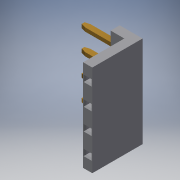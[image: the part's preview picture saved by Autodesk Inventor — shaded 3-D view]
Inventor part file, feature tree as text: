
AUTODESK INVENTOR PART (.ipt)
format: ipt  version: 2018.3 (Build 223284000, 284)  size: 212,992 bytes
history: native  units: mm
features: chamfer x12, extrude x4, sketch x4
ambient origin geometry x8: Origin, YZ Plane, XZ Plane, XY Plane, X Axis, Y Axis, Z Axis, Center Point
bodies: Body1 (feature_tree)
feature tree (20):
  extrude  "Extrusion4"  Depth=1.0mm
  extrude  "Extrusion5"  Depth=1.0mm
  extrude  "Extrusion6"  Depth=3.5mm TaperAngle=0.0deg
  chamfer  "Chamfer5"  Distance=0.6mm
  chamfer  "Chamfer6"  Distance=0.4mm
  chamfer  "Chamfer7"  Distance=0.6mm
  chamfer  "Chamfer8"  Distance=0.4mm
  chamfer  "Chamfer9"  Distance=0.2mm
  chamfer  "Chamfer10"  Distance=0.2mm
  chamfer  "Chamfer11"  Distance=0.2mm
  chamfer  "Chamfer12"  Distance=3.5mm
  extrude  "Extrusion7"  Depth=1.29mm
  chamfer  "Chamfer13"  Distance=1.94mm
  chamfer  "Chamfer14"  Distance=0.4mm
  chamfer  "Chamfer15"  Distance=1.94mm
  chamfer  "Chamfer16"  Distance=1.29mm
  sketch  "Sketch4"  dims[d22=1.5mm d23=1.0mm]
  sketch  "Sketch5"  dims[d24=1.0mm d25=2.0mm]
  sketch  "Sketch6"  dims[d26=10.0mm d27=0.0mm d28=3.5mm d29=0.0mm]
  sketch  "Sketch7"  dims[d30=0.4mm d31=0.6mm d32=0.4mm d33=0.6mm d36=0.4mm d37=0.6mm d38=1.94mm d40=0.2mm d41=0.2mm d42=0.2mm d47=3.5mm d48=0.0mm d49=1.29mm d50=1.94mm d51=0.4mm d52=0.6mm d53=0.2mm d54=1.94mm d55=1.29mm d56=0.15mm d57=0.5mm d58=45.0deg d59=0.15mm d60=0.5mm d61=45.0deg d62=0.15mm d63=0.5mm d64=45.0deg d65=0.15mm d66=0.5mm d67=45.0deg d68=0.15mm d69=0.5mm d70=45.0deg d71=0.15mm d72=0.5mm d73=45.0deg d74=0.15mm d75=0.5mm d76=45.0deg d77=0.15mm d78=0.5mm d79=45.0deg d80=0.2mm d81=0.6mm d82=0.4mm d83=0.4mm d84=0.4mm d85=0.4mm d86=0.2mm d87=3.7mm d88=0.0mm d89=0.15mm d90=0.5mm d91=45.0deg d92=0.15mm d93=0.5mm d94=45.0deg d95=0.15mm d96=0.5mm d97=45.0deg d98=0.15mm d99=0.5mm d100=45.0deg]
